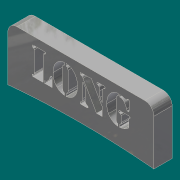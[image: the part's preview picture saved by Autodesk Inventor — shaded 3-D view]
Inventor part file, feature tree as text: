
AUTODESK INVENTOR PART (.ipt)
format: ipt  version: 2017 SP1 (Build 210196100, 196)  size: 335,360 bytes
history: native  units: in
note: dims shown in document units (in); Inventor stores cm internally (conversion verified against a paired STEP export)
features: extrude x2, sketch x2, fillet x1
ambient origin geometry x8: Origin, YZ Plane, XZ Plane, XY Plane, X Axis, Y Axis, Z Axis, Center Point
bodies: Solid1 (feature_tree)
feature tree (5):
  extrude  "Extrusion1"  Depth=1.5in
  extrude  "Extrusion2"  Depth=0.25in TaperAngle=0.0deg
  fillet  "Fillet1"  [1 undecoded]
  sketch  "Sketch1"  dims[d0=4.0in d1=1.5in]
  sketch  "Sketch2"  dims[d2=21.5in d3=0.5in d4=0.0in d5=0.0in d6=0.0in d7=0.25in]
note: 1 required parameter value undecoded (feature->parameter linkage not recoverable at this tier; creation-order binding heuristic only, values carry confidence <= 0.55)
